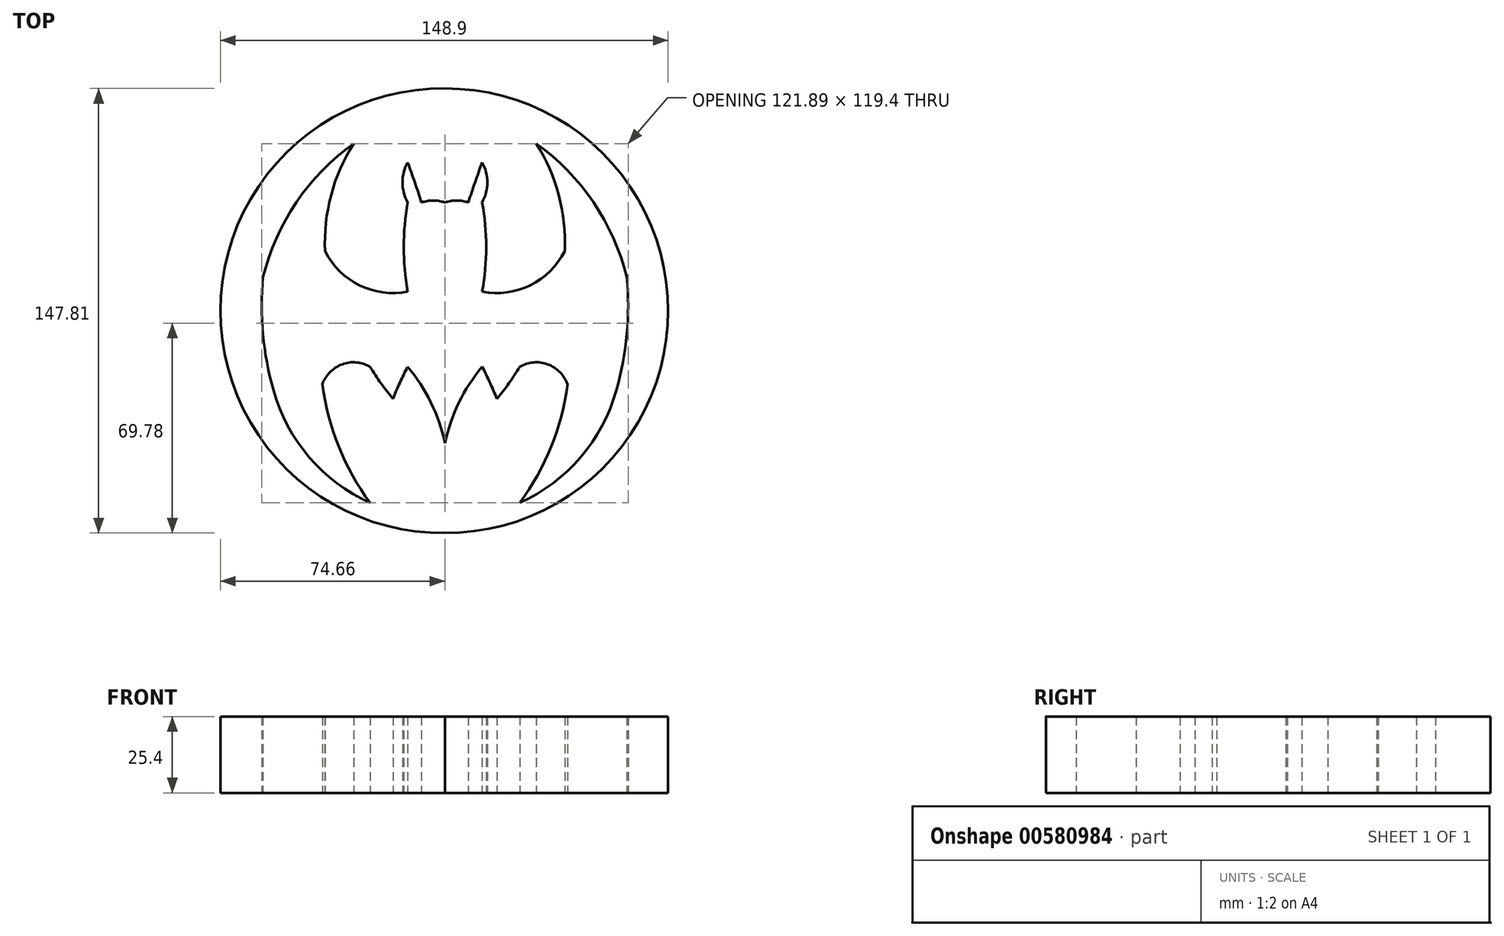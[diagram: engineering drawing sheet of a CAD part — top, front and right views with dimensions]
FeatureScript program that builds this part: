
annotation { "Feature Type Name" : "Feature", "Feature Type Description" : "" }
export const myFeature = defineFeature(function(context is Context, id is Id, definition is map)
    precondition{}
    {
        {
            var Q0;
            Q0=qCreatedBy(makeId("Top.planeOp"),FACE);
            var sketch = newSketch(context, id + "F0", { "sketchPlane" : qUnion([Q0])});
            skArc(sketch, "E0", {"start": v(-60.5, 11.36) * mm, "mid": v(-60.5, -7.6) * mm, "end": v(-57.02, -26.22) * mm});
            skArc(sketch, "E1", {"start": v(-30.39, 55.73) * mm, "mid": v(-49.4, 36.23) * mm, "end": v(-60.5, 11.36) * mm});
            skArc(sketch, "E2", {"start": v(-57.02, -26.22) * mm, "mid": v(-45.14, -48.54) * mm, "end": v(-24.89, -63.67) * mm});
            skArc(sketch, "E3", {"start": v(-30.39, 55.73) * mm, "mid": v(-37.87, 38.6) * mm, "end": v(-39.85, 20) * mm});
            skArc(sketch, "E4", {"start": v(-39.85, 20) * mm, "mid": v(-28.38, 8.63) * mm, "end": v(-12.37, 6.54) * mm});
            skArc(sketch, "E5", {"start": v(-12.37, 36.19) * mm, "mid": v(-13.7, 21.36) * mm, "end": v(-12.37, 6.54) * mm});
            skArc(sketch, "E6", {"start": v(-12.37, 49.48) * mm, "mid": v(-14.11, 42.84) * mm, "end": v(-12.37, 36.19) * mm});
            skArc(sketch, "E7", {"start": v(-7.79, 36.19) * mm, "mid": v(-10.02, 42.85) * mm, "end": v(-12.37, 49.48) * mm});
            skArc(sketch, "E8", {"start": v(0, 36.19) * mm, "mid": v(-3.9, 36.8) * mm, "end": v(-7.79, 36.19) * mm});
            skArc(sketch, "E9", {"start": v(-40.77, -24.28) * mm, "mid": v(-35.34, -44.99) * mm, "end": v(-24.89, -63.67) * mm});
            skArc(sketch, "E10", {"start": v(-24.89, -18.48) * mm, "mid": v(-34.2, -17.65) * mm, "end": v(-40.77, -24.28) * mm});
            skArc(sketch, "E11", {"start": v(-24.89, -18.48) * mm, "mid": v(-21.28, -23.96) * mm, "end": v(-17.28, -29.16) * mm});
            skArc(sketch, "E12", {"start": v(-12.37, -18.48) * mm, "mid": v(-14.98, -23.75) * mm, "end": v(-17.28, -29.16) * mm});
            skArc(sketch, "E13", {"start": v(0, -43.82) * mm, "mid": v(-4.65, -30.4) * mm, "end": v(-12.37, -18.48) * mm});
            skArc(sketch, "E14.MirrorCS", {"start": v(0, 36.19) * mm, "mid": v(3.9, 36.8) * mm, "end": v(7.79, 36.19) * mm});
            skArc(sketch, "E15.MirrorCS", {"start": v(7.79, 36.19) * mm, "mid": v(10.02, 42.85) * mm, "end": v(12.37, 49.48) * mm});
            skArc(sketch, "E16.MirrorCS", {"start": v(12.37, 49.48) * mm, "mid": v(14.11, 42.84) * mm, "end": v(12.37, 36.19) * mm});
            skArc(sketch, "E17.MirrorCS", {"start": v(12.37, 36.19) * mm, "mid": v(13.7, 21.36) * mm, "end": v(12.37, 6.54) * mm});
            skArc(sketch, "E18.MirrorCS", {"start": v(39.85, 20) * mm, "mid": v(28.38, 8.63) * mm, "end": v(12.37, 6.54) * mm});
            skArc(sketch, "E19.MirrorCS", {"start": v(30.39, 55.73) * mm, "mid": v(37.87, 38.6) * mm, "end": v(39.85, 20) * mm});
            skArc(sketch, "E20.MirrorCS", {"start": v(30.39, 55.73) * mm, "mid": v(49.4, 36.23) * mm, "end": v(60.5, 11.36) * mm});
            skArc(sketch, "E21.MirrorCS", {"start": v(60.5, 11.36) * mm, "mid": v(60.5, -7.6) * mm, "end": v(57.02, -26.22) * mm});
            skArc(sketch, "E22.MirrorCS", {"start": v(57.02, -26.22) * mm, "mid": v(45.14, -48.54) * mm, "end": v(24.89, -63.67) * mm});
            skArc(sketch, "E23.MirrorCS", {"start": v(40.77, -24.28) * mm, "mid": v(35.34, -44.99) * mm, "end": v(24.89, -63.67) * mm});
            skArc(sketch, "E24.MirrorCS", {"start": v(24.89, -18.48) * mm, "mid": v(34.2, -17.65) * mm, "end": v(40.77, -24.28) * mm});
            skArc(sketch, "E25.MirrorCS", {"start": v(24.89, -18.48) * mm, "mid": v(21.28, -23.96) * mm, "end": v(17.28, -29.16) * mm});
            skArc(sketch, "E26.MirrorCS", {"start": v(12.37, -18.48) * mm, "mid": v(14.98, -23.75) * mm, "end": v(17.28, -29.16) * mm});
            skArc(sketch, "E27.MirrorCS", {"start": v(0, -43.82) * mm, "mid": v(4.65, -30.4) * mm, "end": v(12.37, -18.48) * mm});
            skArc(sketch, "E28", {"start": v(0, -73.75) * mm, "mid": v(74.24, 0.15) * mm, "end": v(0, 74.06) * mm});
            skArc(sketch, "E29", {"start": v(0, 74.06) * mm, "mid": v(-74.66, 0.15) * mm, "end": v(0, -73.75) * mm});
            skSolve(sketch);
        }
        {
            var Q0;
            Q0 = qSketchRegion(id + "F0", true);
            extrude(context, id + "F1", {"entities" : qUnion([Q0]), "depth" : 25.4 * mm, "offsetDistance" : 25.4 * mm});
        }
    });
